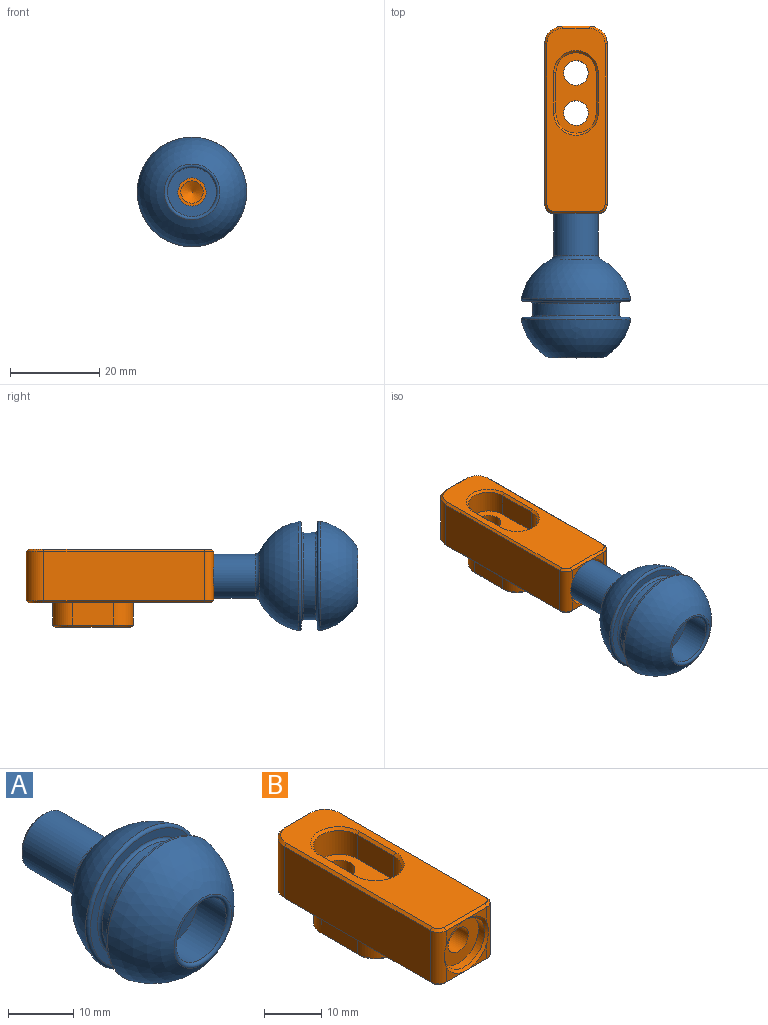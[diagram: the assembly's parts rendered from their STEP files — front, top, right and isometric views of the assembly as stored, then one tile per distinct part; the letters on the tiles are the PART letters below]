
ASSEMBLY  parts=2 mates=1
PART A: 17 faces, bbox 26.6x34.8x26.6 mm
  f0: cylinder r=5mm len=11.36mm, axis (0,-1,0), area 357mm2, adj f15,f16
  f1: sphere r=12.5mm, area 691.3mm2, adj f10,f15
  f2: plane 23.56x23.56mm, normal (0,-1,0), area 105.7mm2, adj f10,f11
  f3: cylinder r=9.75mm len=19.5mm, axis (0,-1,0), area 159.3mm2, adj f11,f12
  f4: plane 23.56x23.56mm, normal (0,1,0), area 105.7mm2, adj f12,f13
  f5: sphere r=12.5mm, area 662.1mm2, adj f13,f14
  f6: cylinder r=5.5mm len=11mm, axis (0,-1,0), area 213.1mm2, adj f7,f14
  f7: plane 11x11mm, normal (0,-1,0), area 63.9mm2, adj f6,f8
  f8: cylinder r=3.15mm len=28.18mm, axis (0,-1,0), area 557.8mm2, adj f7,f9
  f9: plane 9x9mm, normal (0,1,0), area 32.4mm2, adj f8,f16
  f10: torus R=11.78mm, axis (0,-1,0), area 67.1mm2, adj f1,f2
  f11: torus R=10.25mm, axis (0,-1,0), area 49mm2, adj f2,f3
  f12: torus R=10.25mm, axis (0,1,0), area 49mm2, adj f3,f4
  f13: torus R=11.78mm, axis (0,1,0), area 67.1mm2, adj f4,f5
  f14: torus R=6mm, axis (0,1,0), area 38.1mm2, adj f5,f6
  f15: torus R=6mm, axis (0,-1,0), area 36.2mm2, adj f0,f1
  f16: cone r=5mm half-angle=45deg, axis (0,-1,0), area 21.1mm2, adj f0,f9
PART B: 54 faces, bbox 14x42x17.5 mm
  f0: plane 5x3.21mm, normal (0,-1,0), area 4.5mm2, adj f27,f29,f42
  f1: plane 5x3.21mm, normal (0,-1,0), area 4.5mm2, adj f27,f28,f34
  f2: plane 5x3.21mm, normal (0,-1,0), area 4.5mm2, adj f27,f28,f42
  f3: cylinder r=2.75mm len=11.9mm, axis (0,0,1), area 205.6mm2, adj f9,f22
  f4: cylinder r=2.75mm len=11.9mm, axis (0,0,1), area 205.6mm2, adj f9,f22
  f5: plane 9x5mm, normal (1,0,0), area 45mm2, adj f6,f8,f10,f49
  f6: cylinder r=4.5mm len=9mm, axis (0,0,-1), area 70.7mm2, adj f5,f7,f10,f47
  f7: plane 9x5mm, normal (-1,0,0), area 45mm2, adj f6,f8,f10,f46
  f8: cylinder r=4.5mm len=9mm, axis (0,0,-1), area 70.7mm2, adj f5,f7,f10,f48
  f9: plane 17x8mm, normal (0,0,-1), area 74.7mm2, adj f3,f4,f46,f47,f48,f49
  f10: plane 41x13mm, normal (0,0,-1), area 382.2mm2, adj f5,f6,f7,f8,f30,f31,f32,f33
  f11: cylinder r=4mm len=11mm, axis (0,0,-1), area 69.1mm2, adj f12,f16,f31,f39
  f12: plane 36x11mm, normal (-1,0,0), area 396mm2, adj f11,f28,f30,f38
  f13: plane 5x3.21mm, normal (0,-1,0), area 4.5mm2, adj f27,f29,f34
  f14: plane 36x11mm, normal (1,0,0), area 396mm2, adj f15,f29,f37,f45
  f15: cylinder r=4mm len=11mm, axis (0,0,-1), area 69.1mm2, adj f14,f16,f35,f43
  f16: plane 11x6mm, normal (0,1,0), area 66mm2, adj f11,f15,f33,f41
  f17: plane 41x13mm, normal (0,0,1), area 358.2mm2, adj f38,f39,f40,f41,f42,f43,f44,f45
  f18: plane 9x5.1mm, normal (-1,0,0), area 45.9mm2, adj f19,f21,f22,f53
  f19: cylinder r=4.5mm len=9mm, axis (0,0,1), area 72.1mm2, adj f18,f20,f22,f51
  f20: plane 9x5.1mm, normal (1,0,0), area 45.9mm2, adj f19,f21,f22,f50
  f21: cylinder r=4.5mm len=9mm, axis (0,0,1), area 72.1mm2, adj f18,f20,f22,f52
  f22: plane 18x9mm, normal (0,0,1), area 97.1mm2, adj f3,f4,f18,f19,f20,f21
  f23: cylinder r=5mm len=10mm, axis (0,-1,0), area 47.1mm2, adj f24,f27
  f24: plane 10x10mm, normal (0,-1,0), area 58.9mm2, adj f23,f26
  f25: cone r=0mm half-angle=59deg, axis (0,-1,0), area 22.9mm2, adj f26
  f26: cylinder r=2.5mm len=13mm, axis (0,-1,0), area 204.2mm2, adj f24,f25
  f27: cone r=5mm half-angle=45deg, axis (0,-1,0), area 23mm2, adj f0,f1,f2,f13,f23,f28,f29
  f28: cylinder r=2mm len=11mm, axis (0,0,-1), area 33.1mm2, adj f1,f2,f12,f27,f32,f40
  f29: cylinder r=2mm len=11mm, axis (0,0,1), area 33.1mm2, adj f0,f13,f14,f27,f36,f44
  f30: plane 36x0.5mm, normal (-0.71,0,-0.71), area 25.5mm2, adj f10,f12,f31,f32
  f31: cone r=4mm half-angle=45deg, axis (0,0,1), area 4.2mm2, adj f10,f11,f30,f33
  f32: cone r=1.5mm half-angle=45deg, axis (0,0,1), area 1.9mm2, adj f10,f28,f30,f34
  f33: plane 6x0.5mm, normal (0,0.71,-0.71), area 4.2mm2, adj f10,f16,f31,f35
  f34: plane 10x0.5mm, normal (0,-0.71,-0.71), area 7.1mm2, adj f1,f10,f13,f32,f36
  f35: cone r=4mm half-angle=45deg, axis (0,0,1), area 4.2mm2, adj f10,f15,f33,f37
  f36: cone r=1.5mm half-angle=45deg, axis (0,0,1), area 1.9mm2, adj f10,f29,f34,f37
  f37: plane 36x0.5mm, normal (0.71,0,-0.71), area 25.5mm2, adj f10,f14,f35,f36
  f38: plane 36x0.5mm, normal (-0.71,0,0.71), area 25.5mm2, adj f12,f17,f39,f40
  f39: cone r=3.5mm half-angle=45deg, axis (0,0,-1), area 4.2mm2, adj f11,f17,f38,f41
  f40: cone r=1.5mm half-angle=45deg, axis (0,0,-1), area 1.9mm2, adj f17,f28,f38,f42
  f41: plane 6x0.5mm, normal (0,0.71,0.71), area 4.2mm2, adj f16,f17,f39,f43
  f42: plane 10x0.5mm, normal (0,-0.71,0.71), area 7.1mm2, adj f0,f2,f17,f40,f44
  f43: cone r=3.5mm half-angle=45deg, axis (0,0,-1), area 4.2mm2, adj f15,f17,f41,f45
  f44: cone r=1.5mm half-angle=45deg, axis (0,0,-1), area 1.9mm2, adj f17,f29,f42,f45
  f45: plane 36x0.5mm, normal (0.71,0,0.71), area 25.5mm2, adj f14,f17,f43,f44
  f46: plane 9x0.5mm, normal (-0.71,0,-0.71), area 6.4mm2, adj f7,f9,f47,f48
  f47: cone r=4.5mm half-angle=45deg, axis (0,0,1), area 9.4mm2, adj f6,f9,f46,f49
  f48: cone r=4.5mm half-angle=45deg, axis (0,0,1), area 9.4mm2, adj f8,f9,f46,f49
  f49: plane 9x0.5mm, normal (0.71,0,-0.71), area 6.4mm2, adj f5,f9,f47,f48
  f50: plane 9x0.5mm, normal (0.71,0,0.71), area 6.4mm2, adj f17,f20,f51,f52
  f51: cone r=5mm half-angle=45deg, axis (0,0,1), area 10.6mm2, adj f17,f19,f50,f53
  f52: cone r=5mm half-angle=45deg, axis (0,0,1), area 10.6mm2, adj f17,f21,f50,f53
  f53: plane 9x0.5mm, normal (-0.71,0,0.71), area 6.4mm2, adj f17,f18,f51,f52
PLACE A t=(-0.75,-44.3,11.74)mm
PLACE B t=(-0.75,-1.57,0.24)mm
MATE revolute A.f0 <-> B.f23  axis (0,-1,0) through (-0.75,-26.57,11.74)mm
